# Revit family: floodlight_fl_20_midi___pl43_5xa7682d2a4ac_e2b3
name_source: partatom
category: Lighting Fixtures
units: mm (PartAtom-declared; Revit-internal decimal feet)

## family parameters
Cut with Voids When Loaded = No
Host = Face
Light Source = No
Part Type = Normal
Room Calculation Point = No
Round Connector Dimension = Use Diameter
Shared = No

## types (1)
- --- (1 x LED 4000K / CRI = 70 (unbekannt), 19080 lm, 4000K)
    Apparent Load = 142 VA
    CIE Flux Codes = 32 74 99 100 100
    Color Rendering = 70
    Color Temperature = 4000K
    Default Elevation = 1800 mm
    Description = Floodlight FL 20 midi, floodlight, primary light control with lens, of plastic, primary optical cover: protective disc, of toughened safety glass, transparent, light distribution: PL43, light emission: direct distribution, primary light characteristic: asymmetric, installation type: side-entry, post-top, LED, High Power LED, rated luminous flux: 19.080lm, luminous efficacy: 134lm/W, light colour: 740, colour temperature: 4000K, control gear: ECG Plus, control: flexible luminous flux parameterisation, time-dependent luminous flux control, digital communication interface, overheat protection, power reduction, electronic power reduction, with terminal, 5-pole, max. 2.5mm², mains connection: 220..240V, AC, 50/60Hz, rated input power: 142W, LED unit, of diecast aluminium, powder-coated, Siteco® metallic grey (DB 702S), corrosivity category C5 mid according to DIN EN ISO 12944, please order mast flange separately, incl. 1x M20 cable gland for cable Ø 6.5..12mm, inclination adjustable: 0°, 3°, 8°, 15°, length: 862mm, width: 450mm, height: 176mm, housing frame, of diecast aluminium, powder-coated, Siteco® metallic grey (DB 702S), mast flange adapter, of diecast aluminium, powder-coated, Siteco® metallic grey (DB 702S), DALI, protection rating (complete): IP66, insulation class (complete): insulation class II (safety insulation), certification: CE, ENEC, VDE, protection symbol: D, permissible operating ambient temperature: -40..+40°C, permissible operating ambient temperature for outdoor applications: -40..+50°C, standard: DIN EN 12944, packaging unit: 1 piece

Light Distribution: PL43
    Height = 76 mm
    Lamp = 1 x LED 4000K / CRI >= 70 (unbekannt)
    Lamp Light Flux = 19080 lm
    Lamp count = 1
    Length = 862 mm
    Luminous efficacy = 134 lm/W
    Manufacturer = Siteco
    ModVariant = No
    Model = 5XA7682D2A4AC
    Number of Poles = 1
    OnlyDefault = Yes
    Power Factor = 1
    Product Name = Floodlight FL 20 midi | PL43
    Product group = floodlight | pylon top
    ProductGroupID = 6101
    Protection Class = Protection class II
    Protection Degree = IP 66
    RLX_Detail_Level = 1
    RLX_Emergency_Light_Flux = 0 lm
    RLX_Emergency_Type = 0
    RLX_Emergency_Type_DB = No
    RlxData = <blob elided: 117773 chars, md5=f13ccac2>
    Socket = socket
    Standby Power = 0 W
    System Light Flux = 19080 lm
    System Power = 142 W
    Type Comments = factory setting: luminous flux: 100 % | dim-lin: 254 | 489 mA
    Type Image = l_1005941.jpg
    URL = http://relux.com
    VarID = @adj_148583
    Voltage = 0 V
    Weight = 0.00 kg
    Width = 450 mm

## geometry (parser evidence)
native form markers: Sweep x16
no freeform markers — native parametric forms only
